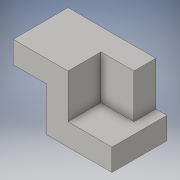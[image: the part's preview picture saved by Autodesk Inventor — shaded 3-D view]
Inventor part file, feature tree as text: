
AUTODESK INVENTOR PART (.ipt)
format: ipt  version: 2016 (Build 200138000, 138)  size: 113,664 bytes
history: native  units: in
note: dims shown in document units (in); Inventor stores cm internally (conversion verified against a paired STEP export)
features: extrude x4, sketch x4
ambient origin geometry x8: Origin, YZ Plane, XZ Plane, XY Plane, X Axis, Y Axis, Z Axis, Center Point
bodies: Solid1 (feature_tree)
feature tree (8):
  extrude  "Extrusion1"  Depth=1.5in
  extrude  "Extrusion2"  Depth=1.0in
  extrude  "Extrusion3"  Depth=0.25in TaperAngle=0.0deg
  extrude  "Extrusion4"  Depth=1.0in
  sketch  "Sketch1"  dims[d0=2.25in d1=1.5in]
  sketch  "Sketch2"  dims[d2=1.25in d3=0.0in d4=1.0in]
  sketch  "Sketch3"  dims[d5=0.5in d6=0.25in d7=0.0in]
  sketch  "Sketch4"  dims[d8=0.75in d9=1.0in d10=1.0in d11=0.0in d12=0.75in d13=1.0in d14=2.0in d15=0.0in]
